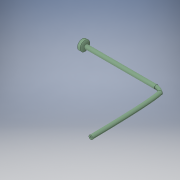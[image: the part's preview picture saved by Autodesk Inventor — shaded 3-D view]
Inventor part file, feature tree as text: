
AUTODESK INVENTOR PART (.ipt)
format: ipt  version: 2019 (Build 230136000, 136)  size: 275,456 bytes
history: native  units: mm
features: sketch x6, sweep x3, extrude x2, revolve x1, plane x1
ambient origin geometry x8: Origin, YZ Plane, XZ Plane, XY Plane, X Axis, Y Axis, Z Axis, Center Point
bodies: Body1 (feature_tree)
feature tree (13):
  revolve  "Revolution2"  [1 undecoded]
  sketch  "Sketch3"  dims[d23=0.0mm d24=0.0mm d25=6.0mm]
  plane  "Work Plane1"
  sketch  "Sketch5"  dims[d26=0.0mm d27=0.0mm d28=6.0mm]
  sweep  "Sweep1"
  sweep  "Sweep2"
  sweep  "Sweep3"
  extrude  "Extrusion1"  [1 undecoded]
  extrude  "Extrusion2"  [1 undecoded]
  sketch  "Sketch2"  dims[d18=90.0deg d22=16.0mm]
  sketch  "Sketch7"  dims[d29=0.0mm d30=0.0mm d31=60.0mm d32=0.0mm]
  sketch  "Sketch8"  dims[d33=250.0mm d34=0.0mm]
  sketch  "Sketch9"
note: 3 required parameter values undecoded (feature->parameter linkage not recoverable at this tier; creation-order binding heuristic only, values carry confidence <= 0.55)